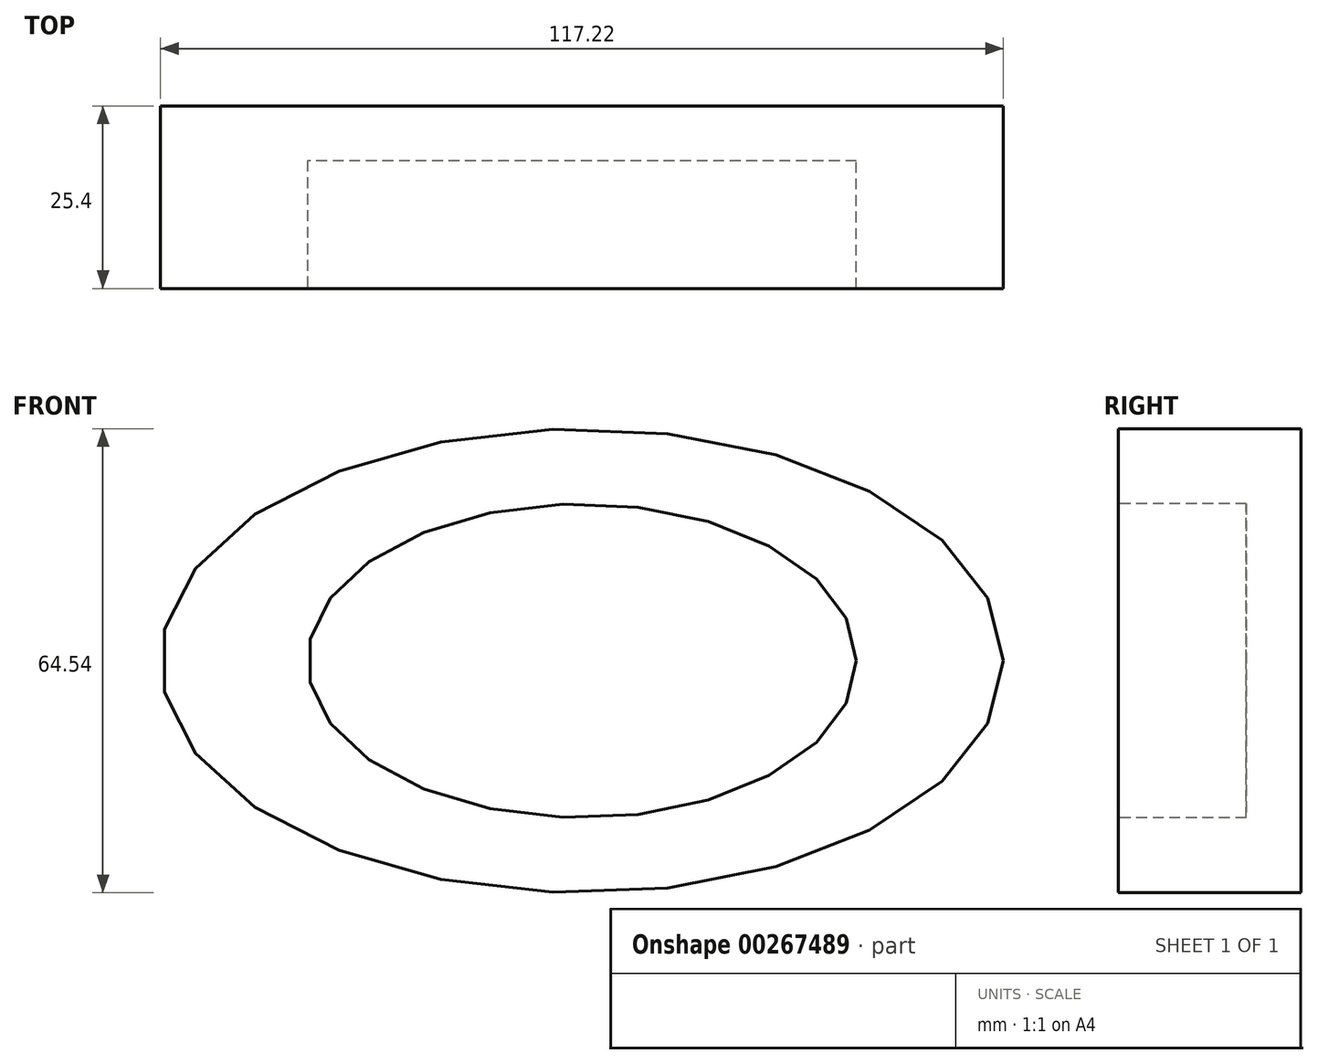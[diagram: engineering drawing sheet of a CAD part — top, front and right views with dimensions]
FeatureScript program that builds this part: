
annotation { "Feature Type Name" : "Feature", "Feature Type Description" : "" }
export const myFeature = defineFeature(function(context is Context, id is Id, definition is map)
    precondition{}
    {
        {
            var Q0;
            Q0=qCreatedBy(makeId("Front.planeOp"),FACE);
            var sketch = newSketch(context, id + "F0", { "sketchPlane" : qUnion([Q0])});
            skEllipse(sketch, "E0", {"center": v(0, 0) * mm, "majorRadius": 58.61 * mm, "minorRadius": 32.27 * mm, "majorAxis": v(1, 0)});
            skEllipse(sketch, "E1", {"center": v(0, 0) * mm, "majorRadius": 38.16 * mm, "minorRadius": 21.83 * mm, "majorAxis": v(1, 0)});
            skSolve(sketch);
        }
        {
            var Q0;
            Q0 = qSketchRegion(id + "F0", true);
            extrude(context, id + "F1", {"entities" : qUnion([Q0]), "depth" : 25.4 * mm});
        }
        {
            var Q0;
            Q0=makeQuery(id+"F0.imprint","IMPRINT",FACE,{"disambiguationData":[TD([[makeQuery(id+"F0.imprint","IMPRINT",EDGE,{"derivedFrom":sQuery(id+"F0.wireOp",EDGE,"E1")}),1.0]])]});
            extrude(context, id + "F2", {"entities" : qUnion([Q0]), "operationType" : NewBodyOperationType.ADD, "depth" : 7.62 * mm});
        }
    });
